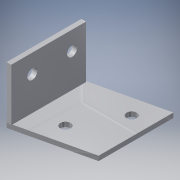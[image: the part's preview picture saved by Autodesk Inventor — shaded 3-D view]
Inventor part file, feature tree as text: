
AUTODESK INVENTOR PART (.ipt)
format: ipt  version: 2016 (Build 200138000, 138)  size: 148,480 bytes
history: native  units: in
note: dims shown in document units (in); Inventor stores cm internally (conversion verified against a paired STEP export)
features: extrude x5, sketch x4
ambient origin geometry x8: Origin, YZ Plane, XZ Plane, XY Plane, X Axis, Y Axis, Z Axis, Center Point
bodies: Solid1 (feature_tree)
feature tree (9):
  extrude  "Extrusion1"  Depth=2.0in
  extrude  "Extrusion2"  Depth=0.9in
  sketch  "Sketch3"  dims[d9=0.9in d12=0.125in d13=0.0in]
  extrude  "Extrusion3"  Depth=0.125in TaperAngle=0.0deg
  extrude  "Extrusion4"  Depth=0.125in
  extrude  "Extrusion5"  Depth=0.125in
  sketch  "Sketch1"  dims[d4=2.0in d5=0.0in d6=0.2656in]
  sketch  "Sketch2"  dims[d7=0.2656in d8=0.9in]
  sketch  "Sketch4"  dims[d14=2.0in d15=0.125in d16=0.5625in d17=1.625in d18=0.0893in d19=0.2656in d20=0.266in d21=0.5in d22=2.0in d23=1.0in d24=0.8619in d26=0.5in d28=0.125in d29=0.0in d30=0.125in d31=0.0in d32=0.475in d33=0.125in d34=0.0in d35=1.883in d36=0.4912in d37=0.7369in]
